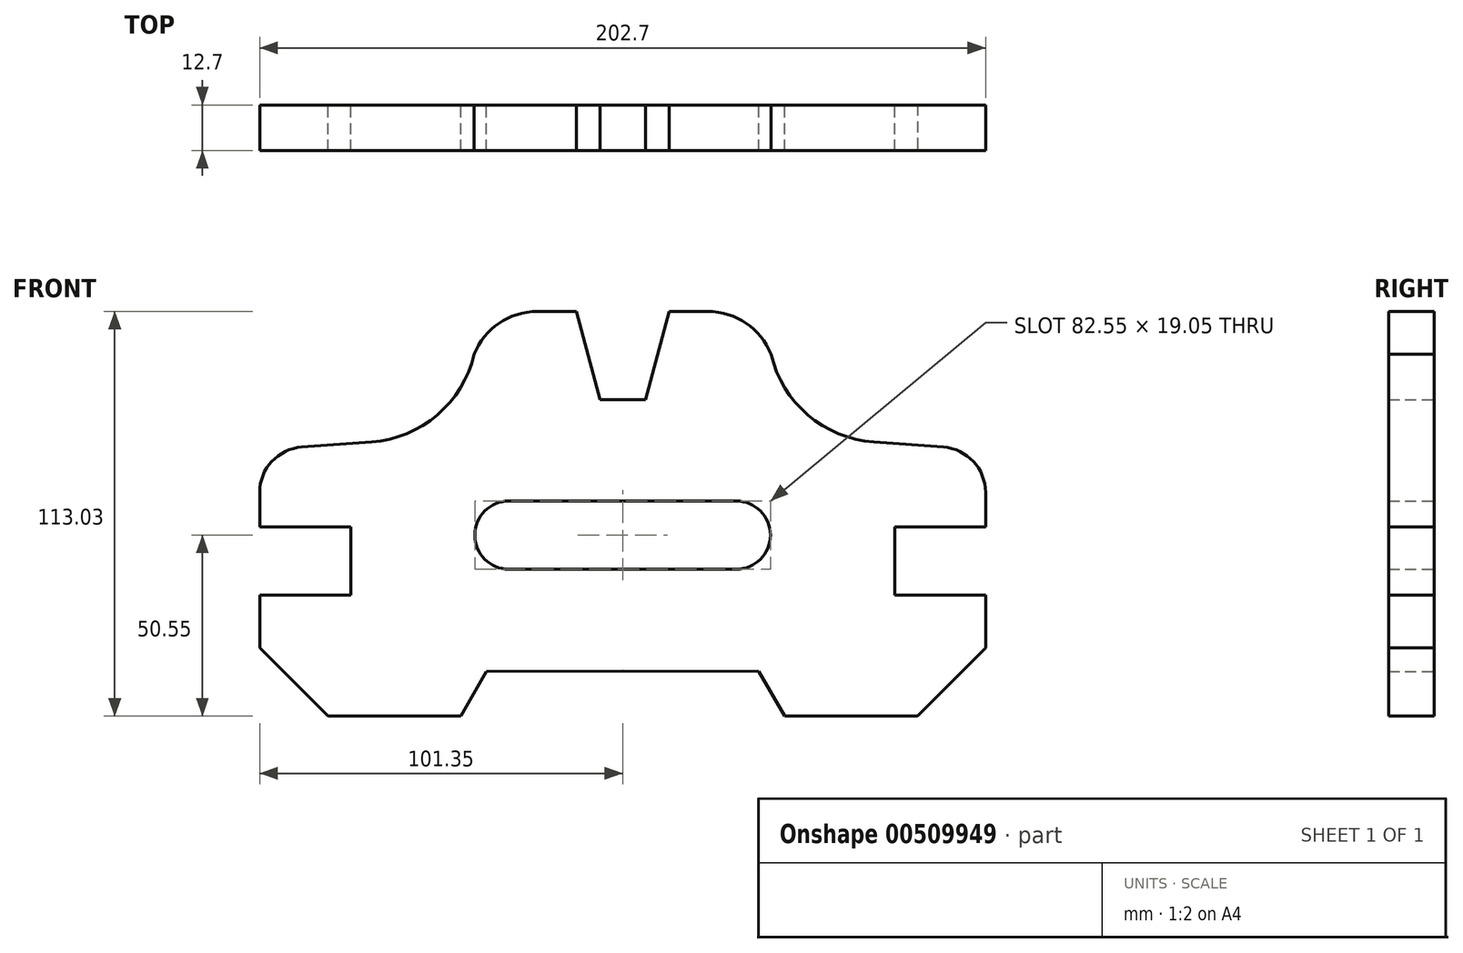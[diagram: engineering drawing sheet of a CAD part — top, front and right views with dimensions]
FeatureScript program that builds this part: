
annotation { "Feature Type Name" : "Feature", "Feature Type Description" : "" }
export const myFeature = defineFeature(function(context is Context, id is Id, definition is map)
    precondition{}
    {
        {
            var Q0;
            Q0=qCreatedBy(makeId("Front.planeOp"),FACE);
            var sketch = newSketch(context, id + "F0", { "sketchPlane" : qUnion([Q0])});
            skLineSegment(sketch, "E0", {"start": v(0, 76.82) * mm, "end": v(0, -77.1) * mm, "construction": true});
            skLineSegment(sketch, "E1", {"start": v(0, 37.85) * mm, "end": v(6.35, 37.85) * mm});
            skLineSegment(sketch, "E2", {"start": v(45.21, -50.55) * mm, "end": v(101.35, -50.55) * mm});
            skLineSegment(sketch, "E3", {"start": v(101.35, -50.55) * mm, "end": v(101.35, -16.76) * mm});
            skLineSegment(sketch, "E4", {"start": v(101.35, -16.76) * mm, "end": v(75.95, -16.76) * mm});
            skLineSegment(sketch, "E5", {"start": v(75.95, -16.76) * mm, "end": v(75.95, 2.29) * mm});
            skLineSegment(sketch, "E6", {"start": v(75.95, 2.29) * mm, "end": v(101.35, 2.29) * mm});
            skLineSegment(sketch, "E7", {"start": v(6.35, 37.85) * mm, "end": v(12.95, 62.48) * mm});
            skLineSegment(sketch, "E8", {"start": v(101.35, 2.29) * mm, "end": v(101.35, 11.94) * mm});
            skArc(sketch, "E9", {"start": v(101.35, 11.94) * mm, "mid": v(97.95, 20.59) * mm, "end": v(89.57, 24.6) * mm});
            skLineSegment(sketch, "E10", {"start": v(89.57, 24.6) * mm, "end": v(70.1, 26.02) * mm});
            skArc(sketch, "E11", {"start": v(70.1, 26.02) * mm, "mid": v(51.76, 33.57) * mm, "end": v(41.48, 50.54) * mm});
            skLineSegment(sketch, "E12", {"start": v(6.35, 37.85) * mm, "end": v(6.35, 78.03) * mm, "construction": true});
            skLineSegment(sketch, "E13.MirrorCS", {"start": v(0, 37.85) * mm, "end": v(-6.35, 37.85) * mm});
            skLineSegment(sketch, "E14.MirrorCS", {"start": v(-6.35, 37.85) * mm, "end": v(-12.95, 62.48) * mm});
            skArc(sketch, "E15.MirrorCS", {"start": v(-70.1, 26.02) * mm, "mid": v(-51.76, 33.57) * mm, "end": v(-41.48, 50.54) * mm});
            skLineSegment(sketch, "E16.MirrorCS", {"start": v(0, -37.93) * mm, "end": v(-38.03, -38.1) * mm});
            skLineSegment(sketch, "E17.MirrorCS", {"start": v(-45.21, -50.55) * mm, "end": v(-101.35, -50.55) * mm});
            skLineSegment(sketch, "E18.MirrorCS", {"start": v(-101.35, -50.55) * mm, "end": v(-101.35, -16.76) * mm});
            skLineSegment(sketch, "E19.MirrorCS", {"start": v(-101.35, -16.76) * mm, "end": v(-75.95, -16.76) * mm});
            skLineSegment(sketch, "E20.MirrorCS", {"start": v(-75.95, -16.76) * mm, "end": v(-75.95, 2.29) * mm});
            skLineSegment(sketch, "E21.MirrorCS", {"start": v(-75.95, 2.29) * mm, "end": v(-101.35, 2.29) * mm});
            skArc(sketch, "E22.MirrorCS", {"start": v(-101.35, 11.94) * mm, "mid": v(-97.95, 20.59) * mm, "end": v(-89.57, 24.6) * mm});
            skLineSegment(sketch, "E23.MirrorCS", {"start": v(-101.35, 2.29) * mm, "end": v(-101.35, 11.94) * mm});
            skLineSegment(sketch, "E24.MirrorCS", {"start": v(-89.57, 24.6) * mm, "end": v(-70.1, 26.02) * mm});
            skLineSegment(sketch, "E25.bottom", {"start": v(31.75, 9.53) * mm, "end": v(-31.75, 9.53) * mm});
            skLineSegment(sketch, "E25.top", {"start": v(31.75, -9.52) * mm, "end": v(-31.75, -9.52) * mm});
            skPoint(sketch, "E25.middle", {"position": v(0, 0) * mm});
            skArc(sketch, "E26", {"start": v(-31.75, 9.53) * mm, "mid": v(-41.28, 0) * mm, "end": v(-31.75, -9.52) * mm});
            skArc(sketch, "E27", {"start": v(31.75, 9.52) * mm, "mid": v(41.27, 0) * mm, "end": v(31.75, -9.52) * mm});
            skLineSegment(sketch, "E28", {"start": v(-38.03, -38.1) * mm, "end": v(-38.03, -66.64) * mm, "construction": true});
            skLineSegment(sketch, "E29", {"start": v(38.03, -38.1) * mm, "end": v(38.03, -76.43) * mm, "construction": true});
            skLineSegment(sketch, "E30", {"start": v(0, -37.93) * mm, "end": v(38.03, -38.1) * mm});
            skLineSegment(sketch, "E31", {"start": v(-45.21, -50.55) * mm, "end": v(-38.03, -38.1) * mm});
            skLineSegment(sketch, "E32", {"start": v(38.03, -38.1) * mm, "end": v(45.21, -50.55) * mm});
            skLineSegment(sketch, "E33", {"start": v(12.95, 62.48) * mm, "end": v(23.8, 62.48) * mm});
            skArc(sketch, "E34", {"start": v(23.8, 62.48) * mm, "mid": v(34.47, 59.22) * mm, "end": v(41.48, 50.54) * mm});
            skLineSegment(sketch, "E35.MirrorCS", {"start": v(-12.95, 62.48) * mm, "end": v(-23.8, 62.48) * mm});
            skArc(sketch, "E36.MirrorCS", {"start": v(-23.8, 62.48) * mm, "mid": v(-34.47, 59.22) * mm, "end": v(-41.48, 50.54) * mm});
            skSolve(sketch);
        }
        {
            var Q0;
            Q0=makeQuery(id+"F0.imprint","IMPRINT",FACE,{"disambiguationData":[TD([[makeQuery(id+"F0.imprint","IMPRINT",EDGE,{"derivedFrom":sQuery(id+"F0.wireOp",EDGE,"E1")}),-1.0]])]});
            extrude(context, id + "F1", {"entities" : qUnion([Q0]), "depth" : 12.7 * mm, "offsetDistance" : 25.4 * mm});
        }
        {
            var Q0;
            Q0=makeQuery(id+"F1.opExtrude","SWEPT_EDGE",EDGE,{"disambiguationData":[OSD([sQuery(id+"F0.wireOp",EDGE,"E17.MirrorCS"),sQuery(id+"F0.wireOp",EDGE,"E18.MirrorCS")])]});
            var Q1;
            Q1=makeQuery(id+"F1.opExtrude","SWEPT_EDGE",EDGE,{"disambiguationData":[OSD([sQuery(id+"F0.wireOp",EDGE,"E2"),sQuery(id+"F0.wireOp",EDGE,"E3")])]});
            chamfer(context, id + "F2", {"entities" : qUnion([Q0, Q1]), "chamferType" : ChamferType.OFFSET_ANGLE, "width" : 19.05 * mm, "oppositeDirection" : false, "angle" : 45 * degree, "tangentPropagation" : true});
        }
    });
